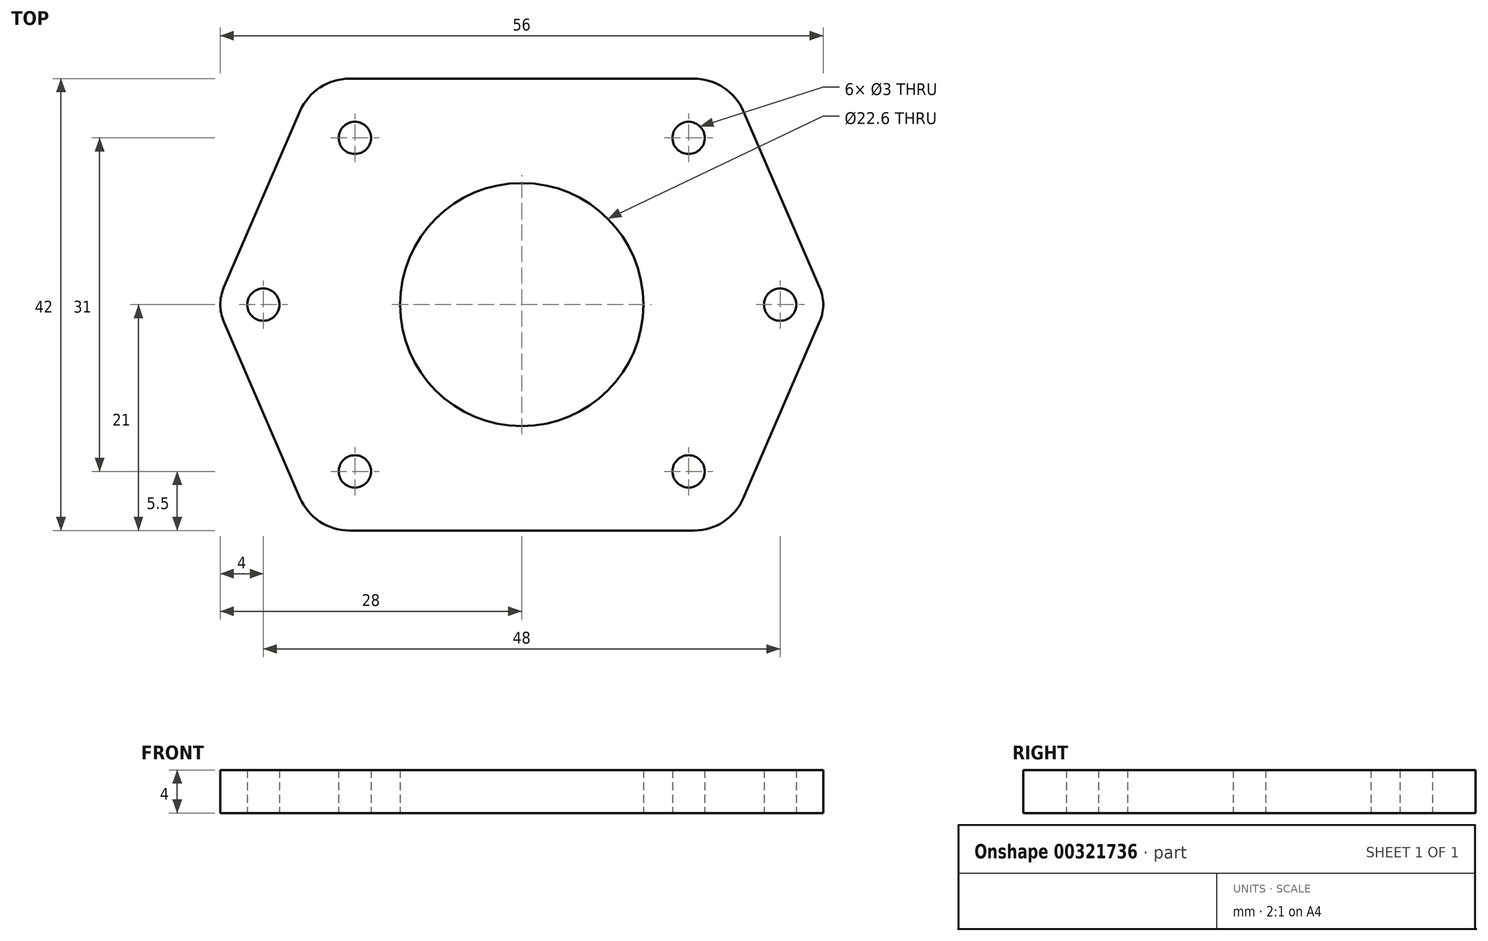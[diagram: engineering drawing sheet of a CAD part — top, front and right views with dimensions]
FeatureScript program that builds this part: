
annotation { "Feature Type Name" : "Feature", "Feature Type Description" : "" }
export const myFeature = defineFeature(function(context is Context, id is Id, definition is map)
    precondition{}
    {
        {
            var Q0;
            Q0=qCreatedBy(makeId("Top.planeOp"),FACE);
            var sketch = newSketch(context, id + "F0", { "sketchPlane" : qUnion([Q0])});
            skLineSegment(sketch, "E0.bottom", {"start": v(-15.5, 15.5) * mm, "end": v(15.5, 15.5) * mm, "construction": true});
            skLineSegment(sketch, "E0.top", {"start": v(-15.5, -15.5) * mm, "end": v(15.5, -15.5) * mm, "construction": true});
            skLineSegment(sketch, "E0.left", {"start": v(-15.5, 15.5) * mm, "end": v(-15.5, -15.5) * mm, "construction": true});
            skLineSegment(sketch, "E0.right", {"start": v(15.5, 15.5) * mm, "end": v(15.5, -15.5) * mm, "construction": true});
            skPoint(sketch, "E0.middle", {"position": v(0, 0) * mm});
            skCircle(sketch, "E1", {"center": v(-15.5, 15.5) * mm, "radius": 1.5 * mm});
            skCircle(sketch, "E2", {"center": v(15.5, 15.5) * mm, "radius": 1.5 * mm});
            skCircle(sketch, "E3", {"center": v(15.5, -15.5) * mm, "radius": 1.5 * mm});
            skCircle(sketch, "E4", {"center": v(-15.5, -15.5) * mm, "radius": 1.5 * mm});
            skCircle(sketch, "E5", {"center": v(0, 0) * mm, "radius": 11.3 * mm});
            skPoint(sketch, "E6.visualSharp", {"position": v(-21, -21) * mm});
            skPoint(sketch, "E7.visualSharp", {"position": v(21, -21) * mm});
            skCircle(sketch, "E8", {"center": v(-24, 0) * mm, "radius": 1.5 * mm});
            skCircle(sketch, "E9", {"center": v(24, 0) * mm, "radius": 1.5 * mm});
            skArc(sketch, "E10", {"start": v(-27.67, 1.59) * mm, "mid": v(-28, 0) * mm, "end": v(-27.67, -1.59) * mm});
            skArc(sketch, "E11", {"start": v(27.67, -1.59) * mm, "mid": v(28, 0) * mm, "end": v(27.67, 1.59) * mm});
            skLineSegment(sketch, "E12.bottom", {"start": v(-16, 21) * mm, "end": v(16, 21) * mm});
            skLineSegment(sketch, "E12.top", {"start": v(-16, -21) * mm, "end": v(16, -21) * mm});
            skPoint(sketch, "E13.visualSharp", {"position": v(-21, 21) * mm});
            skArc(sketch, "E13.filletArc", {"start": v(-16, 21) * mm, "mid": v(-18.75, 20.18) * mm, "end": v(-20.6, 17.98) * mm});
            skPoint(sketch, "E14.visualSharp", {"position": v(21, 21) * mm});
            skArc(sketch, "E14.filletArc", {"start": v(20.6, 17.98) * mm, "mid": v(18.75, 20.18) * mm, "end": v(16, 21) * mm});
            skArc(sketch, "E15.filletArc", {"start": v(16, -21) * mm, "mid": v(18.75, -20.18) * mm, "end": v(20.6, -17.98) * mm});
            skArc(sketch, "E16.filletArc", {"start": v(-20.6, -17.98) * mm, "mid": v(-18.75, -20.18) * mm, "end": v(-16, -21) * mm});
            skLineSegment(sketch, "E17", {"start": v(-20.6, 17.98) * mm, "end": v(-27.67, 1.59) * mm});
            skLineSegment(sketch, "E18", {"start": v(-20.6, -17.98) * mm, "end": v(-27.67, -1.59) * mm});
            skLineSegment(sketch, "E19", {"start": v(20.6, 17.98) * mm, "end": v(27.67, 1.59) * mm});
            skLineSegment(sketch, "E20", {"start": v(27.67, -1.59) * mm, "end": v(20.6, -17.98) * mm});
            skSolve(sketch);
        }
        {
            var Q0;
            Q0=makeQuery(id+"F0.imprint","IMPRINT",FACE,{"disambiguationData":[TD([[makeQuery(id+"F0.imprint","IMPRINT",EDGE,{"derivedFrom":sQuery(id+"F0.wireOp",EDGE,"E1")}),-1.0]])]});
            extrude(context, id + "F1", {"entities" : qUnion([Q0]), "depth" : 4 * mm});
        }
    });
